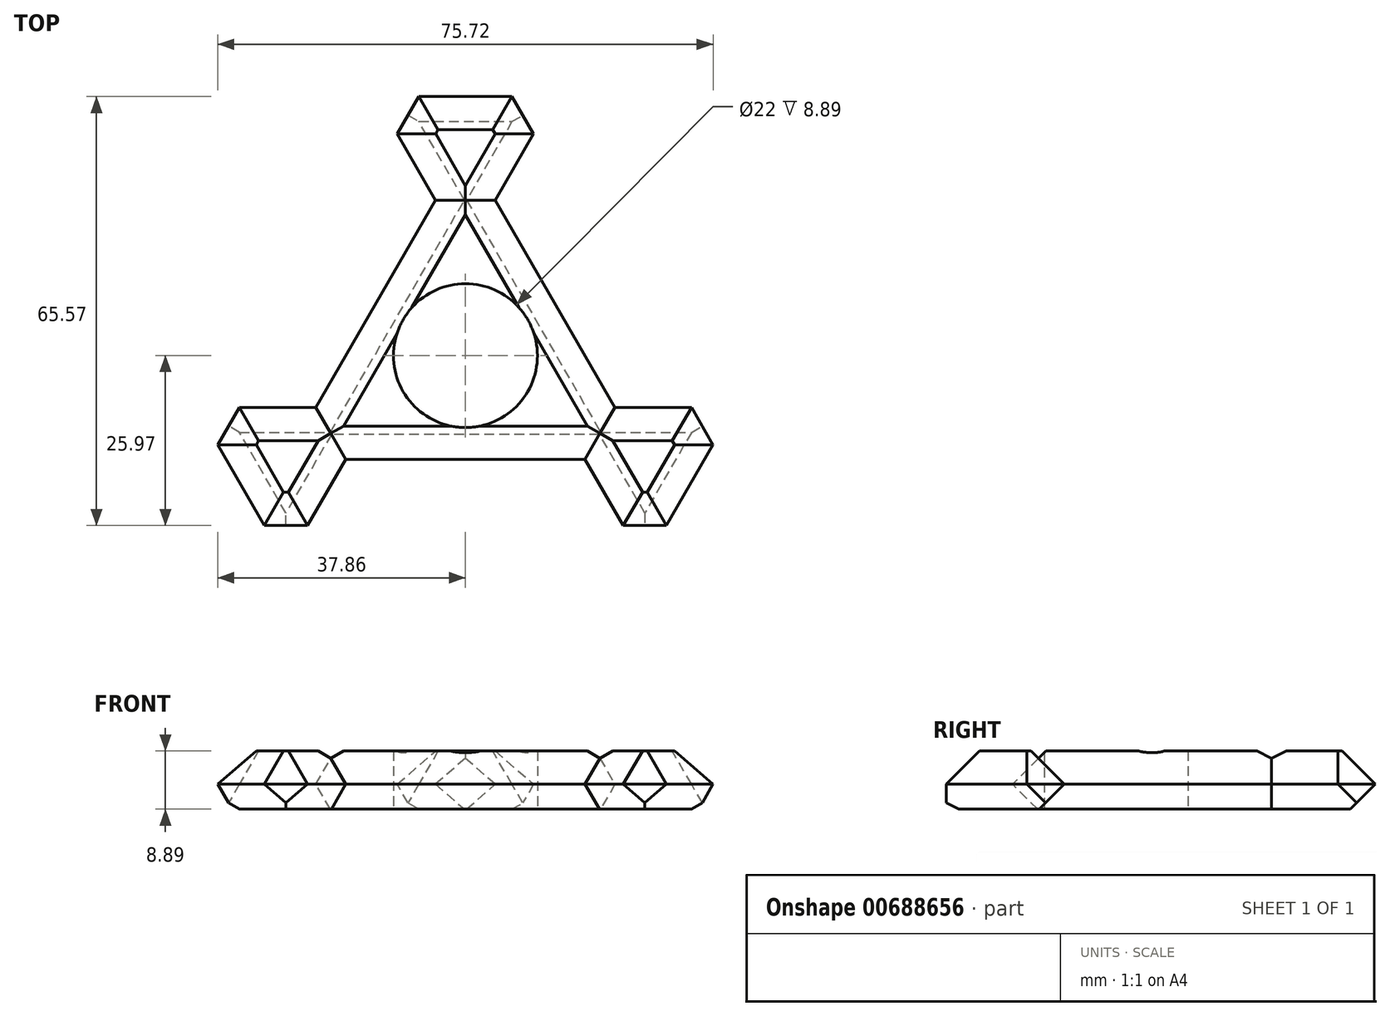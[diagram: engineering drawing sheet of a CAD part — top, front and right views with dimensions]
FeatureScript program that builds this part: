
annotation { "Feature Type Name" : "Feature", "Feature Type Description" : "" }
export const myFeature = defineFeature(function(context is Context, id is Id, definition is map)
    precondition{}
    {
        {
            var Q0;
            Q0=qCreatedBy(makeId("Top.planeOp"),FACE);
            var sketch = newSketch(context, id + "F0", { "sketchPlane" : qUnion([Q0])});
            skCircle(sketch, "E0", {"center": v(0, 0) * mm, "radius": 11 * mm});
            skCircle(sketch, "E1.cCircle", {"center": v(0, 0) * mm, "radius": 31.68 * mm, "construction": true});
            skLineSegment(sketch, "E1.0", {"start": v(0, 31.68) * mm, "end": v(27.44, -15.84) * mm});
            skLineSegment(sketch, "E1.1", {"start": v(27.44, -15.84) * mm, "end": v(-27.44, -15.84) * mm});
            skLineSegment(sketch, "E1.2", {"start": v(-27.44, -15.84) * mm, "end": v(0, 31.68) * mm});
            skLineSegment(sketch, "E2", {"start": v(0, 0) * mm, "end": v(27.44, -15.84) * mm});
            skLineSegment(sketch, "E3", {"start": v(0, 0) * mm, "end": v(0, 31.68) * mm});
            skLineSegment(sketch, "E4", {"start": v(0, 0) * mm, "end": v(-27.44, -15.84) * mm});
            skCircle(sketch, "E5.cCircle", {"center": v(27.44, -15.84) * mm, "radius": 15.84 * mm, "construction": true});
            skLineSegment(sketch, "E5.0", {"start": v(13.72, -7.92) * mm, "end": v(41.16, -7.92) * mm});
            skLineSegment(sketch, "E5.1", {"start": v(41.16, -7.92) * mm, "end": v(27.44, -31.68) * mm});
            skLineSegment(sketch, "E5.2", {"start": v(27.44, -31.68) * mm, "end": v(13.72, -7.92) * mm});
            skCircle(sketch, "E6.cCircle", {"center": v(-27.44, -15.84) * mm, "radius": 15.84 * mm, "construction": true});
            skLineSegment(sketch, "E6.0", {"start": v(-13.72, -7.92) * mm, "end": v(-27.44, -31.68) * mm});
            skLineSegment(sketch, "E6.1", {"start": v(-27.44, -31.68) * mm, "end": v(-41.16, -7.92) * mm});
            skLineSegment(sketch, "E6.2", {"start": v(-41.16, -7.92) * mm, "end": v(-13.72, -7.92) * mm});
            skCircle(sketch, "E7.cCircle", {"center": v(0, 31.68) * mm, "radius": 15.84 * mm, "construction": true});
            skLineSegment(sketch, "E7.0", {"start": v(0, 15.84) * mm, "end": v(-13.72, 39.6) * mm});
            skLineSegment(sketch, "E7.1", {"start": v(-13.72, 39.6) * mm, "end": v(13.72, 39.6) * mm});
            skLineSegment(sketch, "E7.2", {"start": v(13.72, 39.6) * mm, "end": v(0, 15.84) * mm});
            skSolve(sketch);
        }
        {
            var Q0;
            {var subQ1=sQuery(id+"F0.wireOp",EDGE,"E3");var subQ3=sQuery(id+"F0.wireOp",EDGE,"E0");var subQ4=makeQuery(id+"F0.imprint","INTERSECT",VERTEX,{"derivedFrom":[subQ3,subQ1]});Q0=makeQuery(id+"F0.imprint","IMPRINT",FACE,{"disambiguationData":[TD([[makeQuery(id+"F0.imprint","IMPRINT",EDGE,{"disambiguationData":[TD([[subQ4,1.0]])],"derivedFrom":subQ3}),-1.0]])]});}
            var Q1;
            {var subQ1=sQuery(id+"F0.wireOp",EDGE,"E4");var subQ3=sQuery(id+"F0.wireOp",EDGE,"E0");var subQ4=makeQuery(id+"F0.imprint","INTERSECT",VERTEX,{"derivedFrom":[subQ3,subQ1]});Q1=makeQuery(id+"F0.imprint","IMPRINT",FACE,{"disambiguationData":[TD([[makeQuery(id+"F0.imprint","IMPRINT",EDGE,{"disambiguationData":[TD([[subQ4,-1.0]])],"derivedFrom":subQ3}),-1.0]])]});}
            var Q2;
            {var subQ1=sQuery(id+"F0.wireOp",EDGE,"E4");var subQ3=sQuery(id+"F0.wireOp",EDGE,"E0");var subQ4=makeQuery(id+"F0.imprint","INTERSECT",VERTEX,{"derivedFrom":[subQ3,subQ1]});Q2=makeQuery(id+"F0.imprint","IMPRINT",FACE,{"disambiguationData":[TD([[makeQuery(id+"F0.imprint","IMPRINT",EDGE,{"disambiguationData":[TD([[subQ4,1.0]])],"derivedFrom":subQ3}),-1.0]])]});}
            extrude(context, id + "F1", {"entities" : qUnion([Q0, Q1, Q2]), "depth" : 8.9 * mm, "offsetDistance" : 25.4 * mm});
        }
        {
            var Q0;
            Q0 = qSketchRegion(id + "F0", true);
            extrude(context, id + "F2", {"entities" : qUnion([Q0]), "operationType" : NewBodyOperationType.ADD, "depth" : 8.9 * mm, "offsetDistance" : 25.4 * mm});
        }
        {
            var Q0;
            Q0=makeQuery(id+"F2.opExtrude","CAP_EDGE",EDGE,{"disambiguationData":[OSD([sQuery(id+"F0.wireOp",EDGE,"E6.0")])],"isStart":true});
            var Q1;
            Q1=makeQuery(id+"F2.opExtrude","CAP_EDGE",EDGE,{"disambiguationData":[OSD([sQuery(id+"F0.wireOp",EDGE,"E6.1")])],"isStart":true});
            var Q2;
            Q2=makeQuery(id+"F2.opExtrude","CAP_EDGE",EDGE,{"disambiguationData":[OSD([sQuery(id+"F0.wireOp",EDGE,"E6.2")])],"isStart":true});
            var Q3;
            Q3=makeQuery(id+"F1.opExtrude","CAP_EDGE",EDGE,{"disambiguationData":[OSD([sQuery(id+"F0.wireOp",EDGE,"E1.1")])],"isStart":true});
            var Q4;
            Q4=makeQuery(id+"F1.opExtrude","CAP_EDGE",EDGE,{"disambiguationData":[OSD([sQuery(id+"F0.wireOp",EDGE,"E1.2")])],"isStart":true});
            var Q5;
            Q5=makeQuery(id+"F2.opExtrude","CAP_EDGE",EDGE,{"disambiguationData":[OSD([sQuery(id+"F0.wireOp",EDGE,"E7.0")])],"isStart":true});
            var Q6;
            Q6=makeQuery(id+"F2.opExtrude","CAP_EDGE",EDGE,{"disambiguationData":[OSD([sQuery(id+"F0.wireOp",EDGE,"E7.2")])],"isStart":true});
            var Q7;
            Q7=makeQuery(id+"F1.opExtrude","CAP_EDGE",EDGE,{"disambiguationData":[OSD([sQuery(id+"F0.wireOp",EDGE,"E1.0")])],"isStart":true});
            var Q8;
            Q8=makeQuery(id+"F2.opExtrude","CAP_EDGE",EDGE,{"disambiguationData":[OSD([sQuery(id+"F0.wireOp",EDGE,"E5.0")])],"isStart":true});
            var Q9;
            Q9=makeQuery(id+"F2.opExtrude","CAP_EDGE",EDGE,{"disambiguationData":[OSD([sQuery(id+"F0.wireOp",EDGE,"E5.1")])],"isStart":true});
            var Q10;
            Q10=makeQuery(id+"F2.opExtrude","CAP_EDGE",EDGE,{"disambiguationData":[OSD([sQuery(id+"F0.wireOp",EDGE,"E5.2")])],"isStart":true});
            var Q11;
            Q11=makeQuery(id+"F2.opExtrude","CAP_EDGE",EDGE,{"disambiguationData":[OSD([sQuery(id+"F0.wireOp",EDGE,"E7.1")])],"isStart":true});
            chamfer(context, id + "F3", {"entities" : qUnion([Q0, Q1, Q2, Q3, Q4, Q5, Q6, Q7, Q8, Q9, Q10, Q11]), "width" : 3.8 * mm, "tangentPropagation" : true});
        }
        {
            var Q0;
            Q0=makeQuery(id+"F2.opExtrude","SWEPT_EDGE",EDGE,{"disambiguationData":[OSD([sQuery(id+"F0.wireOp",EDGE,"E5.1"),sQuery(id+"F0.wireOp",EDGE,"E5.2")])]});
            var Q1;
            Q1=makeQuery(id+"F2.opExtrude","SWEPT_EDGE",EDGE,{"disambiguationData":[OSD([sQuery(id+"F0.wireOp",EDGE,"E5.0"),sQuery(id+"F0.wireOp",EDGE,"E5.1")])]});
            var Q2;
            Q2=makeQuery(id+"F2.opExtrude","SWEPT_EDGE",EDGE,{"disambiguationData":[OSD([sQuery(id+"F0.wireOp",EDGE,"E7.1"),sQuery(id+"F0.wireOp",EDGE,"E7.2")])]});
            var Q3;
            Q3=makeQuery(id+"F2.opExtrude","SWEPT_EDGE",EDGE,{"disambiguationData":[OSD([sQuery(id+"F0.wireOp",EDGE,"E6.0"),sQuery(id+"F0.wireOp",EDGE,"E6.1")])]});
            var Q4;
            Q4=makeQuery(id+"F2.opExtrude","SWEPT_EDGE",EDGE,{"disambiguationData":[OSD([sQuery(id+"F0.wireOp",EDGE,"E7.0"),sQuery(id+"F0.wireOp",EDGE,"E7.1")])]});
            var Q5;
            Q5=makeQuery(id+"F2.opExtrude","SWEPT_EDGE",EDGE,{"disambiguationData":[OSD([sQuery(id+"F0.wireOp",EDGE,"E6.1"),sQuery(id+"F0.wireOp",EDGE,"E6.2")])]});
            chamfer(context, id + "F4", {"entities" : qUnion([Q0, Q1, Q2, Q3, Q4, Q5]), "width" : 3.8 * mm, "tangentPropagation" : true});
        }
        {
            var Q0;
            Q0=makeQuery(id+"F2.opExtrude","CAP_EDGE",EDGE,{"disambiguationData":[OSD([sQuery(id+"F0.wireOp",EDGE,"E7.1")])],"isStart":false});
            var Q1;
            Q1=makeQuery(id+"F2.opExtrude","CAP_EDGE",EDGE,{"disambiguationData":[OSD([sQuery(id+"F0.wireOp",EDGE,"E7.2")])],"isStart":false});
            var Q2;
            Q2=makeQuery(id+"F2.opExtrude","CAP_EDGE",EDGE,{"disambiguationData":[OSD([sQuery(id+"F0.wireOp",EDGE,"E7.0")])],"isStart":false});
            var Q3;
            Q3=makeQuery(id+"F1.opExtrude","CAP_EDGE",EDGE,{"disambiguationData":[OSD([sQuery(id+"F0.wireOp",EDGE,"E1.2")])],"isStart":false});
            var Q4;
            Q4=makeQuery(id+"F1.opExtrude","CAP_EDGE",EDGE,{"disambiguationData":[OSD([sQuery(id+"F0.wireOp",EDGE,"E1.0")])],"isStart":false});
            var Q5;
            Q5=makeQuery(id+"F2.opExtrude","CAP_EDGE",EDGE,{"disambiguationData":[OSD([sQuery(id+"F0.wireOp",EDGE,"E5.0")])],"isStart":false});
            var Q6;
            Q6=makeQuery(id+"F2.opExtrude","CAP_EDGE",EDGE,{"disambiguationData":[OSD([sQuery(id+"F0.wireOp",EDGE,"E5.1")])],"isStart":false});
            var Q7;
            Q7=makeQuery(id+"F2.opExtrude","CAP_EDGE",EDGE,{"disambiguationData":[OSD([sQuery(id+"F0.wireOp",EDGE,"E5.2")])],"isStart":false});
            var Q8;
            Q8=makeQuery(id+"F1.opExtrude","CAP_EDGE",EDGE,{"disambiguationData":[OSD([sQuery(id+"F0.wireOp",EDGE,"E1.1")])],"isStart":false});
            var Q9;
            Q9=makeQuery(id+"F2.opExtrude","CAP_EDGE",EDGE,{"disambiguationData":[OSD([sQuery(id+"F0.wireOp",EDGE,"E6.0")])],"isStart":false});
            var Q10;
            Q10=makeQuery(id+"F2.opExtrude","CAP_EDGE",EDGE,{"disambiguationData":[OSD([sQuery(id+"F0.wireOp",EDGE,"E6.2")])],"isStart":false});
            var Q11;
            {var subQ0=sQuery(id+"F0.wireOp",EDGE,"E7.2");var subQ1=sQuery(id+"F0.wireOp",EDGE,"E7.0");var subQ2=sQuery(id+"F0.wireOp",EDGE,"E6.2");var subQ3=sQuery(id+"F0.wireOp",EDGE,"E6.1");var subQ4=sQuery(id+"F0.wireOp",EDGE,"E6.0");var subQ5=sQuery(id+"F0.wireOp",EDGE,"E5.2");var subQ6=sQuery(id+"F0.wireOp",EDGE,"E5.0");var subQ7=sQuery(id+"F0.wireOp",EDGE,"E1.2");var subQ8=sQuery(id+"F0.wireOp",EDGE,"E1.1");var subQ9=sQuery(id+"F0.wireOp",EDGE,"E1.0");var subQ10=sQuery(id+"F0.wireOp",EDGE,"E0");Q11=makeQuery(id+"F4.opChamfer","BLEND_EDGE",EDGE,{"blendedFrom":[makeQuery(id+"F2.opExtrude","SWEPT_EDGE",EDGE,{"disambiguationData":[OSD([subQ3,subQ2])]}),makeQuery(id+"F2.boolean.opBoolean","MERGE",FACE,{"derivedFrom":[makeQuery(id+"F1.opExtrude","CAP_FACE",FACE,{"disambiguationData":[OSD([subQ10,subQ9,subQ8,subQ7,subQ6,subQ5,subQ4,subQ2,subQ1,subQ0])],"isStart":false}),makeQuery(id+"F2.opExtrude","CAP_FACE",FACE,{"disambiguationData":[OSD([subQ10,subQ9,subQ8,subQ7,subQ6,sQuery(id+"F0.wireOp",EDGE,"E5.1"),subQ5,subQ4,subQ3,subQ2,subQ1,sQuery(id+"F0.wireOp",EDGE,"E7.1"),subQ0])],"isStart":false})]})],"blendedInto":[makeQuery(id+"F2.boolean.opBoolean","MERGE",FACE,{"derivedFrom":[makeQuery(id+"F1.opExtrude","CAP_FACE",FACE,{"disambiguationData":[OSD([subQ10,subQ9,subQ8,subQ7,subQ6,subQ5,subQ4,subQ2,subQ1,subQ0])],"isStart":false}),makeQuery(id+"F2.opExtrude","CAP_FACE",FACE,{"disambiguationData":[OSD([subQ10,subQ9,subQ8,subQ7,subQ6,sQuery(id+"F0.wireOp",EDGE,"E5.1"),subQ5,subQ4,subQ3,subQ2,subQ1,sQuery(id+"F0.wireOp",EDGE,"E7.1"),subQ0])],"isStart":false})]})]});}
            var Q12;
            Q12=makeQuery(id+"F2.opExtrude","CAP_EDGE",EDGE,{"disambiguationData":[OSD([sQuery(id+"F0.wireOp",EDGE,"E6.1")])],"isStart":false});
            var Q13;
            {var subQ0=sQuery(id+"F0.wireOp",EDGE,"E7.2");var subQ1=sQuery(id+"F0.wireOp",EDGE,"E7.0");var subQ2=sQuery(id+"F0.wireOp",EDGE,"E6.2");var subQ3=sQuery(id+"F0.wireOp",EDGE,"E6.1");var subQ4=sQuery(id+"F0.wireOp",EDGE,"E6.0");var subQ5=sQuery(id+"F0.wireOp",EDGE,"E5.2");var subQ6=sQuery(id+"F0.wireOp",EDGE,"E5.0");var subQ7=sQuery(id+"F0.wireOp",EDGE,"E1.2");var subQ8=sQuery(id+"F0.wireOp",EDGE,"E1.1");var subQ9=sQuery(id+"F0.wireOp",EDGE,"E1.0");var subQ10=sQuery(id+"F0.wireOp",EDGE,"E0");Q13=makeQuery(id+"F4.opChamfer","BLEND_EDGE",EDGE,{"blendedFrom":[makeQuery(id+"F2.opExtrude","SWEPT_EDGE",EDGE,{"disambiguationData":[OSD([subQ4,subQ3])]}),makeQuery(id+"F2.boolean.opBoolean","MERGE",FACE,{"derivedFrom":[makeQuery(id+"F1.opExtrude","CAP_FACE",FACE,{"disambiguationData":[OSD([subQ10,subQ9,subQ8,subQ7,subQ6,subQ5,subQ4,subQ2,subQ1,subQ0])],"isStart":false}),makeQuery(id+"F2.opExtrude","CAP_FACE",FACE,{"disambiguationData":[OSD([subQ10,subQ9,subQ8,subQ7,subQ6,sQuery(id+"F0.wireOp",EDGE,"E5.1"),subQ5,subQ4,subQ3,subQ2,subQ1,sQuery(id+"F0.wireOp",EDGE,"E7.1"),subQ0])],"isStart":false})]})],"blendedInto":[makeQuery(id+"F2.boolean.opBoolean","MERGE",FACE,{"derivedFrom":[makeQuery(id+"F1.opExtrude","CAP_FACE",FACE,{"disambiguationData":[OSD([subQ10,subQ9,subQ8,subQ7,subQ6,subQ5,subQ4,subQ2,subQ1,subQ0])],"isStart":false}),makeQuery(id+"F2.opExtrude","CAP_FACE",FACE,{"disambiguationData":[OSD([subQ10,subQ9,subQ8,subQ7,subQ6,sQuery(id+"F0.wireOp",EDGE,"E5.1"),subQ5,subQ4,subQ3,subQ2,subQ1,sQuery(id+"F0.wireOp",EDGE,"E7.1"),subQ0])],"isStart":false})]})]});}
            var Q14;
            {var subQ0=sQuery(id+"F0.wireOp",EDGE,"E7.2");var subQ1=sQuery(id+"F0.wireOp",EDGE,"E7.0");var subQ2=sQuery(id+"F0.wireOp",EDGE,"E6.2");var subQ3=sQuery(id+"F0.wireOp",EDGE,"E6.0");var subQ4=sQuery(id+"F0.wireOp",EDGE,"E5.2");var subQ5=sQuery(id+"F0.wireOp",EDGE,"E5.1");var subQ6=sQuery(id+"F0.wireOp",EDGE,"E5.0");var subQ7=sQuery(id+"F0.wireOp",EDGE,"E1.2");var subQ8=sQuery(id+"F0.wireOp",EDGE,"E1.1");var subQ9=sQuery(id+"F0.wireOp",EDGE,"E1.0");var subQ10=sQuery(id+"F0.wireOp",EDGE,"E0");Q14=makeQuery(id+"F4.opChamfer","BLEND_EDGE",EDGE,{"blendedFrom":[makeQuery(id+"F2.opExtrude","SWEPT_EDGE",EDGE,{"disambiguationData":[OSD([subQ5,subQ4])]}),makeQuery(id+"F2.boolean.opBoolean","MERGE",FACE,{"derivedFrom":[makeQuery(id+"F1.opExtrude","CAP_FACE",FACE,{"disambiguationData":[OSD([subQ10,subQ9,subQ8,subQ7,subQ6,subQ4,subQ3,subQ2,subQ1,subQ0])],"isStart":false}),makeQuery(id+"F2.opExtrude","CAP_FACE",FACE,{"disambiguationData":[OSD([subQ10,subQ9,subQ8,subQ7,subQ6,subQ5,subQ4,subQ3,sQuery(id+"F0.wireOp",EDGE,"E6.1"),subQ2,subQ1,sQuery(id+"F0.wireOp",EDGE,"E7.1"),subQ0])],"isStart":false})]})],"blendedInto":[makeQuery(id+"F2.boolean.opBoolean","MERGE",FACE,{"derivedFrom":[makeQuery(id+"F1.opExtrude","CAP_FACE",FACE,{"disambiguationData":[OSD([subQ10,subQ9,subQ8,subQ7,subQ6,subQ4,subQ3,subQ2,subQ1,subQ0])],"isStart":false}),makeQuery(id+"F2.opExtrude","CAP_FACE",FACE,{"disambiguationData":[OSD([subQ10,subQ9,subQ8,subQ7,subQ6,subQ5,subQ4,subQ3,sQuery(id+"F0.wireOp",EDGE,"E6.1"),subQ2,subQ1,sQuery(id+"F0.wireOp",EDGE,"E7.1"),subQ0])],"isStart":false})]})]});}
            var Q15;
            {var subQ0=sQuery(id+"F0.wireOp",EDGE,"E7.2");var subQ1=sQuery(id+"F0.wireOp",EDGE,"E7.0");var subQ2=sQuery(id+"F0.wireOp",EDGE,"E6.2");var subQ3=sQuery(id+"F0.wireOp",EDGE,"E6.0");var subQ4=sQuery(id+"F0.wireOp",EDGE,"E5.2");var subQ5=sQuery(id+"F0.wireOp",EDGE,"E5.1");var subQ6=sQuery(id+"F0.wireOp",EDGE,"E5.0");var subQ7=sQuery(id+"F0.wireOp",EDGE,"E1.2");var subQ8=sQuery(id+"F0.wireOp",EDGE,"E1.1");var subQ9=sQuery(id+"F0.wireOp",EDGE,"E1.0");var subQ10=sQuery(id+"F0.wireOp",EDGE,"E0");Q15=makeQuery(id+"F4.opChamfer","BLEND_EDGE",EDGE,{"blendedFrom":[makeQuery(id+"F2.opExtrude","SWEPT_EDGE",EDGE,{"disambiguationData":[OSD([subQ6,subQ5])]}),makeQuery(id+"F2.boolean.opBoolean","MERGE",FACE,{"derivedFrom":[makeQuery(id+"F1.opExtrude","CAP_FACE",FACE,{"disambiguationData":[OSD([subQ10,subQ9,subQ8,subQ7,subQ6,subQ4,subQ3,subQ2,subQ1,subQ0])],"isStart":false}),makeQuery(id+"F2.opExtrude","CAP_FACE",FACE,{"disambiguationData":[OSD([subQ10,subQ9,subQ8,subQ7,subQ6,subQ5,subQ4,subQ3,sQuery(id+"F0.wireOp",EDGE,"E6.1"),subQ2,subQ1,sQuery(id+"F0.wireOp",EDGE,"E7.1"),subQ0])],"isStart":false})]})],"blendedInto":[makeQuery(id+"F2.boolean.opBoolean","MERGE",FACE,{"derivedFrom":[makeQuery(id+"F1.opExtrude","CAP_FACE",FACE,{"disambiguationData":[OSD([subQ10,subQ9,subQ8,subQ7,subQ6,subQ4,subQ3,subQ2,subQ1,subQ0])],"isStart":false}),makeQuery(id+"F2.opExtrude","CAP_FACE",FACE,{"disambiguationData":[OSD([subQ10,subQ9,subQ8,subQ7,subQ6,subQ5,subQ4,subQ3,sQuery(id+"F0.wireOp",EDGE,"E6.1"),subQ2,subQ1,sQuery(id+"F0.wireOp",EDGE,"E7.1"),subQ0])],"isStart":false})]})]});}
            var Q16;
            {var subQ0=sQuery(id+"F0.wireOp",EDGE,"E7.2");var subQ1=sQuery(id+"F0.wireOp",EDGE,"E7.1");var subQ2=sQuery(id+"F0.wireOp",EDGE,"E7.0");var subQ3=sQuery(id+"F0.wireOp",EDGE,"E6.2");var subQ4=sQuery(id+"F0.wireOp",EDGE,"E6.0");var subQ5=sQuery(id+"F0.wireOp",EDGE,"E5.2");var subQ6=sQuery(id+"F0.wireOp",EDGE,"E5.0");var subQ7=sQuery(id+"F0.wireOp",EDGE,"E1.2");var subQ8=sQuery(id+"F0.wireOp",EDGE,"E1.1");var subQ9=sQuery(id+"F0.wireOp",EDGE,"E1.0");var subQ10=sQuery(id+"F0.wireOp",EDGE,"E0");Q16=makeQuery(id+"F4.opChamfer","BLEND_EDGE",EDGE,{"blendedFrom":[makeQuery(id+"F2.opExtrude","SWEPT_EDGE",EDGE,{"disambiguationData":[OSD([subQ1,subQ0])]}),makeQuery(id+"F2.boolean.opBoolean","MERGE",FACE,{"derivedFrom":[makeQuery(id+"F1.opExtrude","CAP_FACE",FACE,{"disambiguationData":[OSD([subQ10,subQ9,subQ8,subQ7,subQ6,subQ5,subQ4,subQ3,subQ2,subQ0])],"isStart":false}),makeQuery(id+"F2.opExtrude","CAP_FACE",FACE,{"disambiguationData":[OSD([subQ10,subQ9,subQ8,subQ7,subQ6,sQuery(id+"F0.wireOp",EDGE,"E5.1"),subQ5,subQ4,sQuery(id+"F0.wireOp",EDGE,"E6.1"),subQ3,subQ2,subQ1,subQ0])],"isStart":false})]})],"blendedInto":[makeQuery(id+"F2.boolean.opBoolean","MERGE",FACE,{"derivedFrom":[makeQuery(id+"F1.opExtrude","CAP_FACE",FACE,{"disambiguationData":[OSD([subQ10,subQ9,subQ8,subQ7,subQ6,subQ5,subQ4,subQ3,subQ2,subQ0])],"isStart":false}),makeQuery(id+"F2.opExtrude","CAP_FACE",FACE,{"disambiguationData":[OSD([subQ10,subQ9,subQ8,subQ7,subQ6,sQuery(id+"F0.wireOp",EDGE,"E5.1"),subQ5,subQ4,sQuery(id+"F0.wireOp",EDGE,"E6.1"),subQ3,subQ2,subQ1,subQ0])],"isStart":false})]})]});}
            var Q17;
            {var subQ0=sQuery(id+"F0.wireOp",EDGE,"E7.2");var subQ1=sQuery(id+"F0.wireOp",EDGE,"E7.1");var subQ2=sQuery(id+"F0.wireOp",EDGE,"E7.0");var subQ3=sQuery(id+"F0.wireOp",EDGE,"E6.2");var subQ4=sQuery(id+"F0.wireOp",EDGE,"E6.0");var subQ5=sQuery(id+"F0.wireOp",EDGE,"E5.2");var subQ6=sQuery(id+"F0.wireOp",EDGE,"E5.0");var subQ7=sQuery(id+"F0.wireOp",EDGE,"E1.2");var subQ8=sQuery(id+"F0.wireOp",EDGE,"E1.1");var subQ9=sQuery(id+"F0.wireOp",EDGE,"E1.0");var subQ10=sQuery(id+"F0.wireOp",EDGE,"E0");Q17=makeQuery(id+"F4.opChamfer","BLEND_EDGE",EDGE,{"blendedFrom":[makeQuery(id+"F2.opExtrude","SWEPT_EDGE",EDGE,{"disambiguationData":[OSD([subQ2,subQ1])]}),makeQuery(id+"F2.boolean.opBoolean","MERGE",FACE,{"derivedFrom":[makeQuery(id+"F1.opExtrude","CAP_FACE",FACE,{"disambiguationData":[OSD([subQ10,subQ9,subQ8,subQ7,subQ6,subQ5,subQ4,subQ3,subQ2,subQ0])],"isStart":false}),makeQuery(id+"F2.opExtrude","CAP_FACE",FACE,{"disambiguationData":[OSD([subQ10,subQ9,subQ8,subQ7,subQ6,sQuery(id+"F0.wireOp",EDGE,"E5.1"),subQ5,subQ4,sQuery(id+"F0.wireOp",EDGE,"E6.1"),subQ3,subQ2,subQ1,subQ0])],"isStart":false})]})],"blendedInto":[makeQuery(id+"F2.boolean.opBoolean","MERGE",FACE,{"derivedFrom":[makeQuery(id+"F1.opExtrude","CAP_FACE",FACE,{"disambiguationData":[OSD([subQ10,subQ9,subQ8,subQ7,subQ6,subQ5,subQ4,subQ3,subQ2,subQ0])],"isStart":false}),makeQuery(id+"F2.opExtrude","CAP_FACE",FACE,{"disambiguationData":[OSD([subQ10,subQ9,subQ8,subQ7,subQ6,sQuery(id+"F0.wireOp",EDGE,"E5.1"),subQ5,subQ4,sQuery(id+"F0.wireOp",EDGE,"E6.1"),subQ3,subQ2,subQ1,subQ0])],"isStart":false})]})]});}
            chamfer(context, id + "F5", {"entities" : qUnion([Q0, Q1, Q2, Q3, Q4, Q5, Q6, Q7, Q8, Q9, Q10, Q11, Q12, Q13, Q14, Q15, Q16, Q17]), "width" : 5.08 * mm, "tangentPropagation" : true});
        }
    });
